# Revit family: LiquidSoapDispenserHolder-Vitra-SentoKidsSeries-A4491567
name_source: partatom
category: Plumbing Fixtures
revit_build: Autodesk Revit 2017 (Build: 20160225_1515(x64)
units: mm (PartAtom-declared; Revit-internal decimal feet)

## family parameters
Cut with Voids When Loaded = No
Host = Face
OmniClass Number = 23.45.00.00
OmniClass Title = Sanitary, Laundry, and Cleaning Equipment
Part Type = Normal
Room Calculation Point = No
Round Connector Dimension = Use Diameter
Shared = Yes

## types (1)
- LiquidSoapDispenserHolder-Vitra-SentoKidsSeries-A4491567
    Article No. (default) = A4491567
    BIMobject category = Sanitary - Accessories
    Brand = VitrA
    CW Connection = No
    Coating Material = Orange
    Color = Orange
    Default Elevation = 0 mm  [stored 0 ft]
    Description = Sento Kids Liquid Soap Dispenser Holder
    Design country = Turkey
    HW Connection = No
    IFC Classification = Sanitary Terminal
    Main Material = Metal
    Manufacturer = Vitra
    Manufacturer name = Vitra
    Masterformat 2014 Code = 01 52 19
    Masterformat 2014 Description = Sanitary Facilities
    Model = A4491567
    Mounting type = Wall Mounted
    NBS Referans Code = 31-75
    NBS Referans Description = Sanitary Accessories
    Nominal Depth (mm) = 98 mm
    Nominal Height (mm) = 125 mm
    Nominal Width (mm) = 84 mm  [stored 0.275591 ft]
    OmniClass Code = 23-21 43 15 23
    OmniClass Description = Lotion Dispensers
    Product SKU = A4491567
    Product Type = Built-in Liquid Soap Dispenser Holder
    Product certification = https://www.vitraglobal.com
    Product family = Sento Kids Series
    Product group = Liquid Soap Dispenser Holder
    Product url = https://www.vitra.com.tr
    Secondary Material = Grey
    Technical description = https://www.vitra.com.tr
    UNSPSC Description = Sanitary ware
    URL = https://vitraglobal.com
    Uniclass 1.4 Code = L8244
    Uniclass 1.4 Description = Sanitary dispensers
    Uniclass 2.0 Code = PR-31-75
    Uniclass 2.0 Description = Sanitary Accessories
    Uniclass 2015 Code = Pr_40_70_22
    Uniclass 2015 Name = Dispensers and acceptance units
    Uniformat II Description = FURNISHINGS
    Vent Connection = No
    Warranty Period (Year) = 5 years
    Waste Connection = No
    Weight Net (kg) = 0.35
    Youtube = https://www.youtube.com

note: [stored X ft] marks values corroborated as IEEE doubles in the binary element streams (Revit-internal decimal feet)

## geometry (parser evidence)
native form markers: Sweep x1
no freeform markers — native parametric forms only
